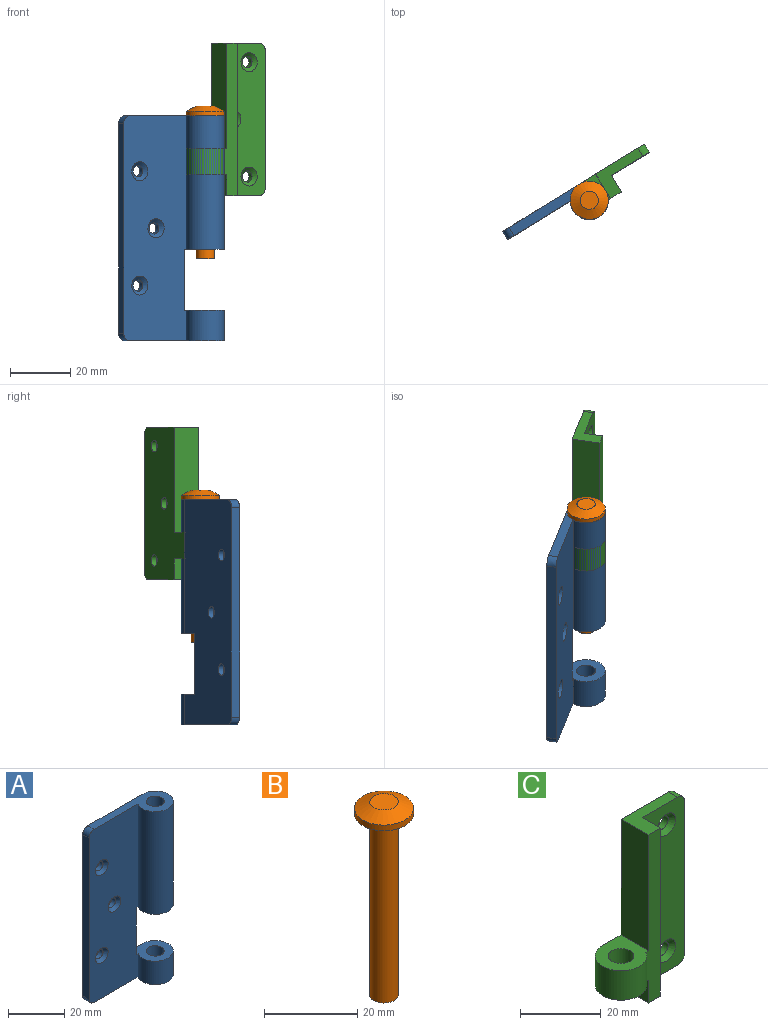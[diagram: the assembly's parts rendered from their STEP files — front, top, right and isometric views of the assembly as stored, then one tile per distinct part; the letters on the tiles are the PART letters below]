
ASSEMBLY  parts=3 mates=3
PART A: 20 faces, bbox 36.4x12.7x75 mm
  f0: plane 75x30mm, normal (0,1,0), area 2084mm2, adj f2,f3,f4,f5,f8,f9,f10,f11
  f1: cylinder r=3.17mm len=10.16mm, axis (0,0,1), area 202.7mm2, adj f4,f13
  f2: cylinder r=6.35mm len=12.7mm, axis (0,0,1), area 337.8mm2, adj f0,f4,f6,f13
  f3: plane 69.92x3.18mm, normal (-1,0,0), area 222mm2, adj f0,f6,f9,f10
  f4: plane 33.81x12.7mm, normal (0,0,-1), area 169.8mm2, adj f0,f1,f2,f6,f9
  f5: plane 33.81x12.7mm, normal (0,0,1), area 169.8mm2, adj f0,f6,f7,f8,f10
  f6: plane 75x24.5mm, normal (0,-1,0), area 1722.5mm2, adj f2,f3,f4,f5,f8,f9,f10,f11
  f7: cylinder r=3.17mm len=44.52mm, axis (0,0,1), area 888.1mm2, adj f5,f11
  f8: cylinder r=6.35mm len=44.52mm, axis (0,0,1), area 1480.2mm2, adj f0,f5,f6,f11
  f9: cylinder r=2.54mm len=3.18mm, axis (0,1,0), area 12.7mm2, adj f0,f3,f4,f6
  f10: cylinder r=2.54mm len=3.18mm, axis (0,-1,0), area 12.7mm2, adj f0,f3,f5,f6
  f11: plane 12.7x12.7mm, normal (0,0,-1), area 102.8mm2, adj f0,f6,f7,f8,f12
  f12: plane 20.32x3.18mm, normal (1,0,0), area 64.5mm2, adj f0,f6,f11,f13
  f13: plane 12.7x12.7mm, normal (0,0,1), area 102.8mm2, adj f0,f1,f2,f6,f12
  f14: cylinder r=1.91mm len=3.81mm, axis (0,-1,0), area 22.8mm2, adj f0,f15
  f15: cone r=1.91mm half-angle=45deg, axis (0,-1,0), area 28.7mm2, adj f6,f14
  f16: cylinder r=1.91mm len=3.81mm, axis (0,-1,0), area 22.8mm2, adj f0,f17
  f17: cone r=1.91mm half-angle=45deg, axis (0,-1,0), area 28.7mm2, adj f6,f16
  f18: cylinder r=1.91mm len=3.81mm, axis (0,-1,0), area 22.8mm2, adj f0,f19
  f19: cone r=1.91mm half-angle=45deg, axis (0,-1,0), area 28.7mm2, adj f6,f18
PART B: 6 faces, bbox 12.7x12.7x50.8 mm
  f0: cylinder r=6.35mm len=12.7mm, axis (0,0,-1), area 60mm2, adj f1,f5
  f1: plane 12.7x12.7mm, normal (0,0,-1), area 97.5mm2, adj f0,f2
  f2: cylinder r=3.05mm len=47.63mm, axis (0,0,-1), area 912.1mm2, adj f1,f3
  f3: plane 6.1x6.1mm, normal (0,0,-1), area 29.2mm2, adj f2
  f4: plane 6.1x6.1mm, normal (0,0,1), area 29.2mm2, adj f5
  f5: cone r=3.05mm half-angle=63.2deg, axis (0,0,-1), area 109.3mm2, adj f0,f4
PART C: 22 faces, bbox 31.8x12.7x50.8 mm
  f0: plane 50.8x14.83mm, normal (0,-1,0), area 659mm2, adj f3,f4,f5,f7,f14,f16,f19,f20
  f1: plane 50.8x25.4mm, normal (0,1,0), area 987.2mm2, adj f3,f4,f5,f6,f8,f9,f10,f11
  f2: plane 50.8x5.07mm, normal (0,-1,0), area 221.9mm2, adj f3,f5,f6,f7,f8,f9,f10,f11
  f3: plane 16.51x9.53mm, normal (0,0,-1), area 79.2mm2, adj f0,f1,f2,f7,f9,f20
  f4: plane 45.72x3.18mm, normal (1,0,0), area 145.2mm2, adj f0,f1,f20,f21
  f5: plane 16.51x9.53mm, normal (0,0,1), area 79.2mm2, adj f0,f1,f2,f7,f10,f21
  f6: cylinder r=6.35mm len=12.7mm, axis (0,0,1), area 236.5mm2, adj f1,f2,f8,f11
  f7: plane 50.8x6.35mm, normal (1,0,0), area 322.6mm2, adj f0,f2,f3,f5,f17
  f8: plane 12.7x12.7mm, normal (0,0,-1), area 104.5mm2, adj f1,f2,f6,f9,f12
  f9: plane 9.53x6.92mm, normal (-1,0,0), area 65.9mm2, adj f1,f2,f3,f8
  f10: plane 35x9.53mm, normal (-1,0,0), area 333.3mm2, adj f1,f2,f5,f11
  f11: plane 12.7x12.7mm, normal (0,0,1), area 104.5mm2, adj f1,f2,f6,f10,f12
  f12: cylinder r=3.17mm len=8.89mm, axis (0,0,1), area 177.3mm2, adj f8,f11
  f13: cylinder r=1.91mm len=3.81mm, axis (0,-1,0), area 22.8mm2, adj f1,f14
  f14: cone r=1.91mm half-angle=45deg, axis (0,-1,0), area 28.7mm2, adj f0,f13
  f15: cylinder r=1.91mm len=3.81mm, axis (0,-1,0), area 22.8mm2, adj f1,f16
  f16: cone r=1.91mm half-angle=45deg, axis (0,-1,0), area 28.7mm2, adj f0,f15,f17
  f17: plane 4.71x1.04mm, normal (0,1,0), area 3.4mm2, adj f7,f16
  f18: cylinder r=1.91mm len=3.81mm, axis (0,-1,0), area 22.8mm2, adj f1,f19
  f19: cone r=1.91mm half-angle=45deg, axis (0,-1,0), area 28.7mm2, adj f0,f18
  f20: cylinder r=2.54mm len=3.18mm, axis (0,-1,0), area 12.7mm2, adj f0,f1,f3,f4
  f21: cylinder r=2.54mm len=3.18mm, axis (0,1,0), area 12.7mm2, adj f0,f1,f4,f5
PLACE A rot(axis=(0,0,1),31.7deg) t=(8.02,4.16,32.9)mm fixed
PLACE B rot(axis=(0,0,1),121.4deg) t=(-2.43,-6.7,31.11)mm
PLACE C rot(axis=(0,0,1),31.4deg) t=(-7.47,-5.39,57.1)mm
MATE planar B.f0 <-> A.f5  axis (0,0,-1) through (-1.07,-8.92,95.13)mm
MATE cylindrical B.f0 <-> A.f1  axis (0,0,-1) through (-1.07,-8.92,71.32)mm
MATE slider B.f0 <-> C.f6  axis (0,0,-1) through (-1.07,-8.92,71.32)mm
